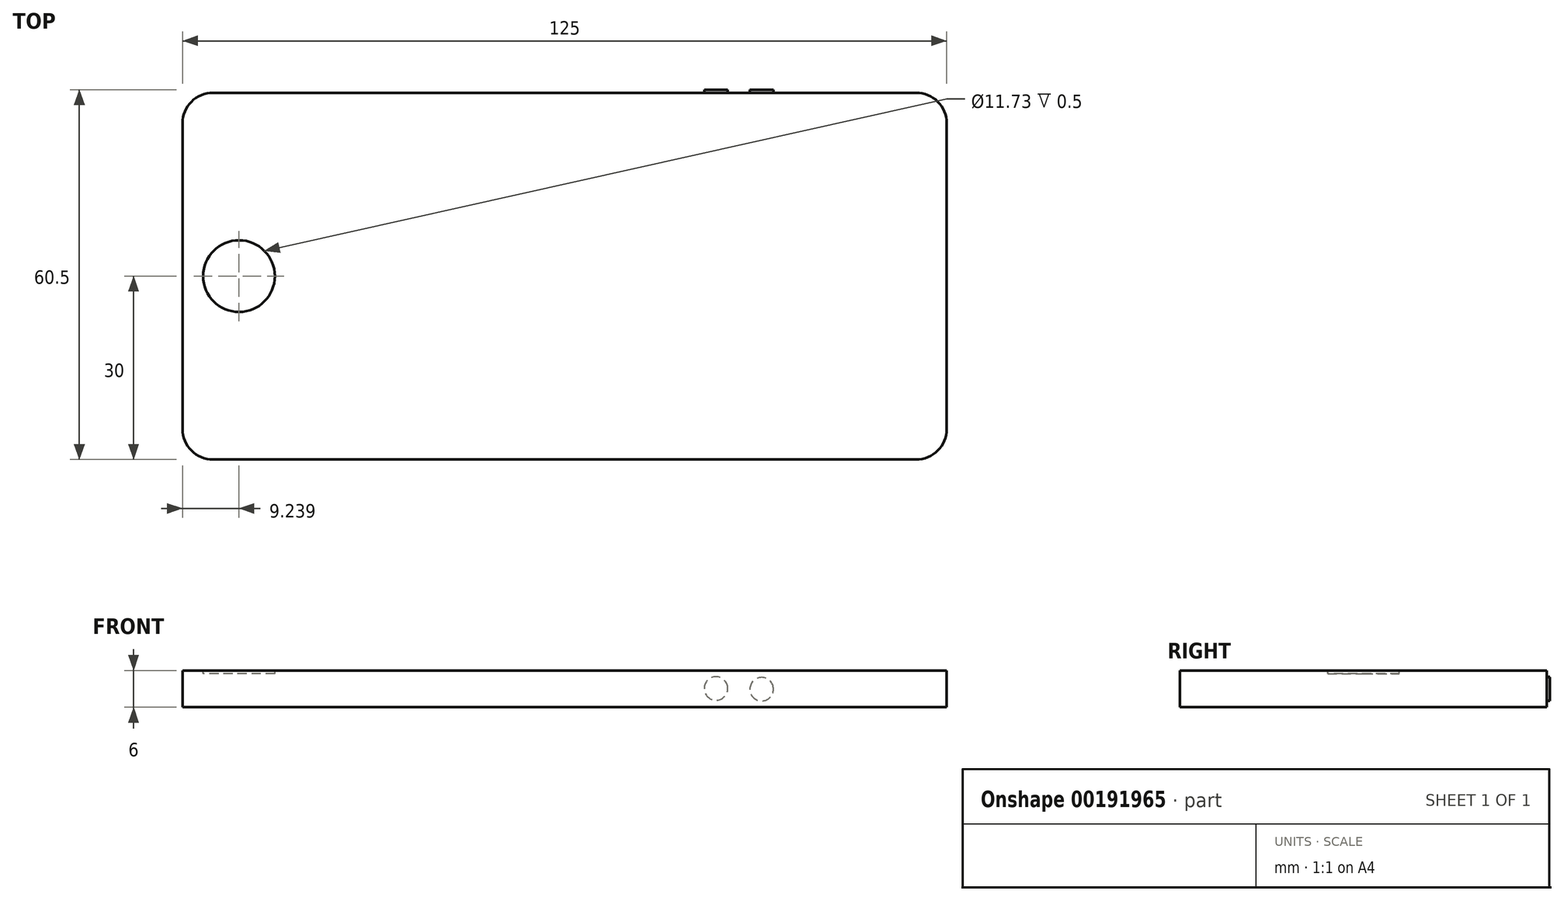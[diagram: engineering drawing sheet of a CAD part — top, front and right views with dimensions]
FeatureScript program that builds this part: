
annotation { "Feature Type Name" : "Feature", "Feature Type Description" : "" }
export const myFeature = defineFeature(function(context is Context, id is Id, definition is map)
    precondition{}
    {
        {
            var Q0;
            Q0=qCreatedBy(makeId("Top.planeOp"),FACE);
            var sketch = newSketch(context, id + "F0", { "sketchPlane" : qUnion([Q0])});
            skLineSegment(sketch, "E0.bottom", {"start": v(-62.5, 30) * mm, "end": v(62.5, 30) * mm});
            skLineSegment(sketch, "E0.top", {"start": v(-62.5, -30) * mm, "end": v(62.5, -30) * mm});
            skLineSegment(sketch, "E0.left", {"start": v(-62.5, 30) * mm, "end": v(-62.5, -30) * mm});
            skLineSegment(sketch, "E0.right", {"start": v(62.5, 30) * mm, "end": v(62.5, -30) * mm});
            skPoint(sketch, "E0.middle", {"position": v(0, 0) * mm});
            skSolve(sketch);
        }
        {
            var Q0;
            Q0=makeQuery(id+"F0.imprint","IMPRINT",FACE,{"disambiguationData":[TD([[makeQuery(id+"F0.imprint","IMPRINT",EDGE,{"derivedFrom":sQuery(id+"F0.wireOp",EDGE,"E0.bottom")}),-1.0]])]});
            extrude(context, id + "F1", {"entities" : qUnion([Q0]), "depth" : 6 * mm});
        }
        {
            var Q0;
            Q0=makeQuery(id+"F1.opExtrude","SWEPT_EDGE",EDGE,{"disambiguationData":[OSD([sQuery(id+"F0.wireOp",EDGE,"E0.bottom"),sQuery(id+"F0.wireOp",EDGE,"E0.left")])]});
            var Q1;
            Q1=makeQuery(id+"F1.opExtrude","SWEPT_EDGE",EDGE,{"disambiguationData":[OSD([sQuery(id+"F0.wireOp",EDGE,"E0.bottom"),sQuery(id+"F0.wireOp",EDGE,"E0.right")])]});
            var Q2;
            Q2=makeQuery(id+"F1.opExtrude","SWEPT_EDGE",EDGE,{"disambiguationData":[OSD([sQuery(id+"F0.wireOp",EDGE,"E0.top"),sQuery(id+"F0.wireOp",EDGE,"E0.right")])]});
            fillet(context, id + "F2", {"entities" : qUnion([Q0, Q1, Q2]), "radius" : 5 * mm, "tangentPropagation" : true, "allowEdgeOverflow" : false});
        }
        {
            var Q0;
            Q0=makeQuery(id+"F1.opExtrude","SWEPT_EDGE",EDGE,{"disambiguationData":[OSD([sQuery(id+"F0.wireOp",EDGE,"E0.top"),sQuery(id+"F0.wireOp",EDGE,"E0.left")])]});
            fillet(context, id + "F3", {"entities" : qUnion([Q0]), "radius" : 5 * mm, "tangentPropagation" : true, "allowEdgeOverflow" : false});
        }
        {
            var Q0;
            Q0=makeQuery(id+"F1.opExtrude","SWEPT_FACE",FACE,{"disambiguationData":[OSD([sQuery(id+"F0.wireOp",EDGE,"E0.bottom")])]});
            var sketch = newSketch(context, id + "F4", { "sketchPlane" : qUnion([Q0])});
            skCircle(sketch, "E1", {"center": v(-32.24, 2.95) * mm, "radius": 1.93 * mm});
            skSolve(sketch);
        }
        {
            var Q0;
            Q0 = qSketchRegion(id + "F4", true);
            extrude(context, id + "F5", {"entities" : qUnion([Q0]), "operationType" : NewBodyOperationType.ADD, "depth" : 0.5 * mm});
        }
        {
            var Q0;
            Q0=makeQuery(id+"F1.opExtrude","SWEPT_FACE",FACE,{"disambiguationData":[OSD([sQuery(id+"F0.wireOp",EDGE,"E0.bottom")])]});
            var sketch = newSketch(context, id + "F6", { "sketchPlane" : qUnion([Q0])});
            skCircle(sketch, "E2", {"center": v(-24.76, 3.06) * mm, "radius": 1.93 * mm});
            skSolve(sketch);
        }
        {
            var Q0;
            Q0 = qSketchRegion(id + "F6", true);
            extrude(context, id + "F7", {"entities" : qUnion([Q0]), "operationType" : NewBodyOperationType.ADD, "depth" : 0.5 * mm});
        }
        {
            var Q0;
            Q0=makeQuery(id+"F1.opExtrude","CAP_FACE",FACE,{"disambiguationData":[OSD([sQuery(id+"F0.wireOp",EDGE,"E0.bottom"),sQuery(id+"F0.wireOp",EDGE,"E0.top"),sQuery(id+"F0.wireOp",EDGE,"E0.left"),sQuery(id+"F0.wireOp",EDGE,"E0.right")])],"isStart":false});
            var sketch = newSketch(context, id + "F8", { "sketchPlane" : qUnion([Q0])});
            skCircle(sketch, "E3", {"center": v(-53.26, 0) * mm, "radius": 5.86 * mm});
            skSolve(sketch);
        }
        {
            var Q0;
            Q0 = qSketchRegion(id + "F8", true);
            extrude(context, id + "F9", {"entities" : qUnion([Q0]), "operationType" : NewBodyOperationType.REMOVE, "oppositeDirection" : true, "depth" : 0.5 * mm});
        }
    });
